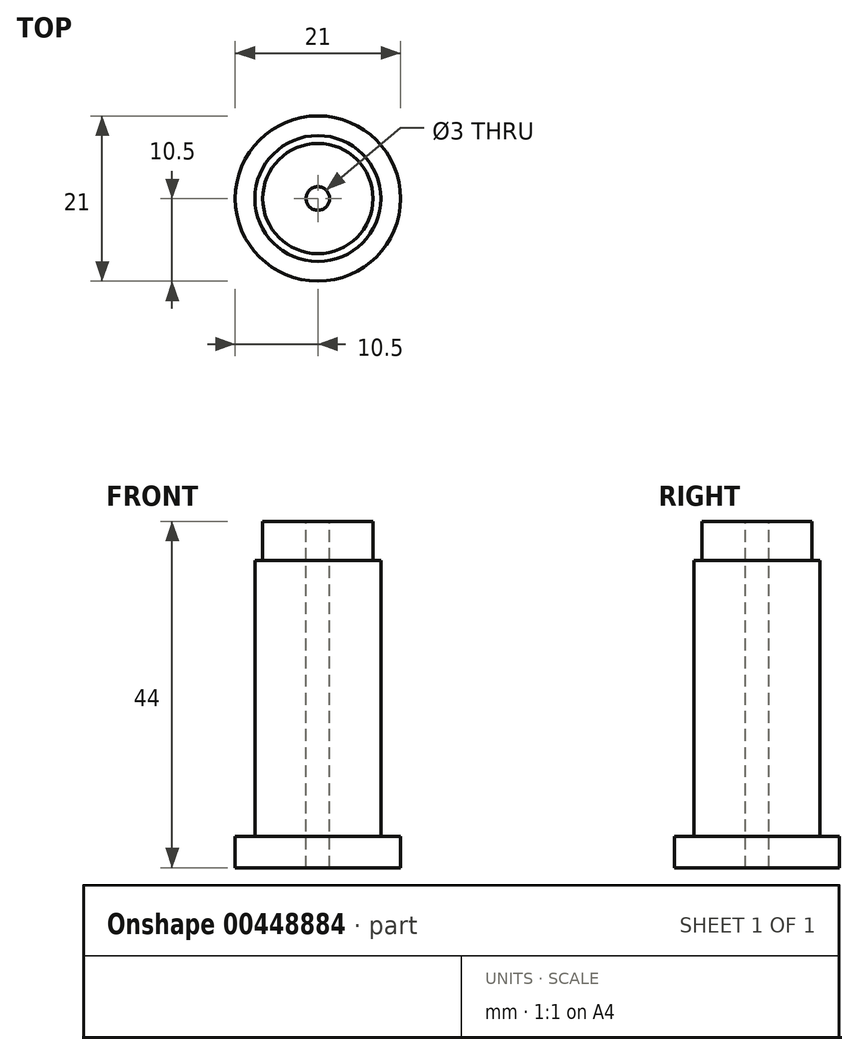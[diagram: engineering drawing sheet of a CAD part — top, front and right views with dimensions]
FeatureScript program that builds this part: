
annotation { "Feature Type Name" : "Feature", "Feature Type Description" : "" }
export const myFeature = defineFeature(function(context is Context, id is Id, definition is map)
    precondition{}
    {
        {
            var Q0;
            Q0=qCreatedBy(makeId("Top.planeOp"),FACE);
            var sketch = newSketch(context, id + "F0", { "sketchPlane" : qUnion([Q0])});
            skCircle(sketch, "E0", {"center": v(0, 0) * mm, "radius": 10.5 * mm});
            skSolve(sketch);
        }
        {
            var Q0;
            Q0=qSketchRegion(id+"F0",true);
            extrude(context, id + "F1", {"entities" : qUnion([Q0]), "depth" : 4 * mm});
        }
        {
            var Q0;
            Q0=qCreatedBy(makeId("Top.planeOp"),FACE);
            var sketch = newSketch(context, id + "F2", { "sketchPlane" : qUnion([Q0])});
            skCircle(sketch, "E1", {"center": v(0, 0) * mm, "radius": 8 * mm});
            skSolve(sketch);
        }
        {
            var Q0;
            Q0=qSketchRegion(id+"F2",true);
            extrude(context, id + "F3", {"entities" : qUnion([Q0]), "operationType" : NewBodyOperationType.ADD, "depth" : 39 * mm});
        }
        {
            var Q0;
            Q0=qCreatedBy(makeId("Right.planeOp"),FACE);
            var sketch = newSketch(context, id + "F4", { "sketchPlane" : qUnion([Q0])});
            skLineSegment(sketch, "E2", {"start": v(0, 44) * mm, "end": v(0, 39) * mm});
            skLineSegment(sketch, "E3", {"start": v(0, 39) * mm, "end": v(7, 39) * mm});
            skLineSegment(sketch, "E4", {"start": v(7, 39) * mm, "end": v(7, 44) * mm});
            skLineSegment(sketch, "E5", {"start": v(7, 44) * mm, "end": v(0, 44) * mm});
            skSolve(sketch);
        }
        {
            var Q0;
            Q0=makeQuery(id+"F4.imprint","IMPRINT",FACE,{"disambiguationData":[TD([[makeQuery(id+"F4.imprint","IMPRINT",EDGE,{"derivedFrom":sQuery(id+"F4.wireOp",EDGE,"E2")}),1.0]])]});
            var Q1;
            Q1=sQuery(id+"F4.wireOp",EDGE,"E2");
            revolve(context, id + "F5", {"operationType" : NewBodyOperationType.ADD, "entities" : qUnion([Q0]), "axis" : qUnion([Q1]), "revolveType" : RevolveType.FULL});
        }
        {
            var Q0;
            Q0=makeQuery(id+"F5.opRevolve","SWEPT_FACE",FACE,{"disambiguationData":[OSD([sQuery(id+"F4.wireOp",EDGE,"E5")])]});
            var sketch = newSketch(context, id + "F6", { "sketchPlane" : qUnion([Q0])});
            skCircle(sketch, "E6", {"center": v(0, 0) * mm, "radius": 1.5 * mm});
            skSolve(sketch);
        }
        {
            var Q0;
            Q0=makeQuery(id+"F6.imprint","IMPRINT",FACE,{"disambiguationData":[TD([[makeQuery(id+"F6.imprint","IMPRINT",EDGE,{"derivedFrom":sQuery(id+"F6.wireOp",EDGE,"E6")}),1.0]])]});
            extrude(context, id + "F7", {"entities" : qUnion([Q0]), "operationType" : NewBodyOperationType.REMOVE, "oppositeDirection" : true, "depth" : 47.7 * mm});
        }
    });
